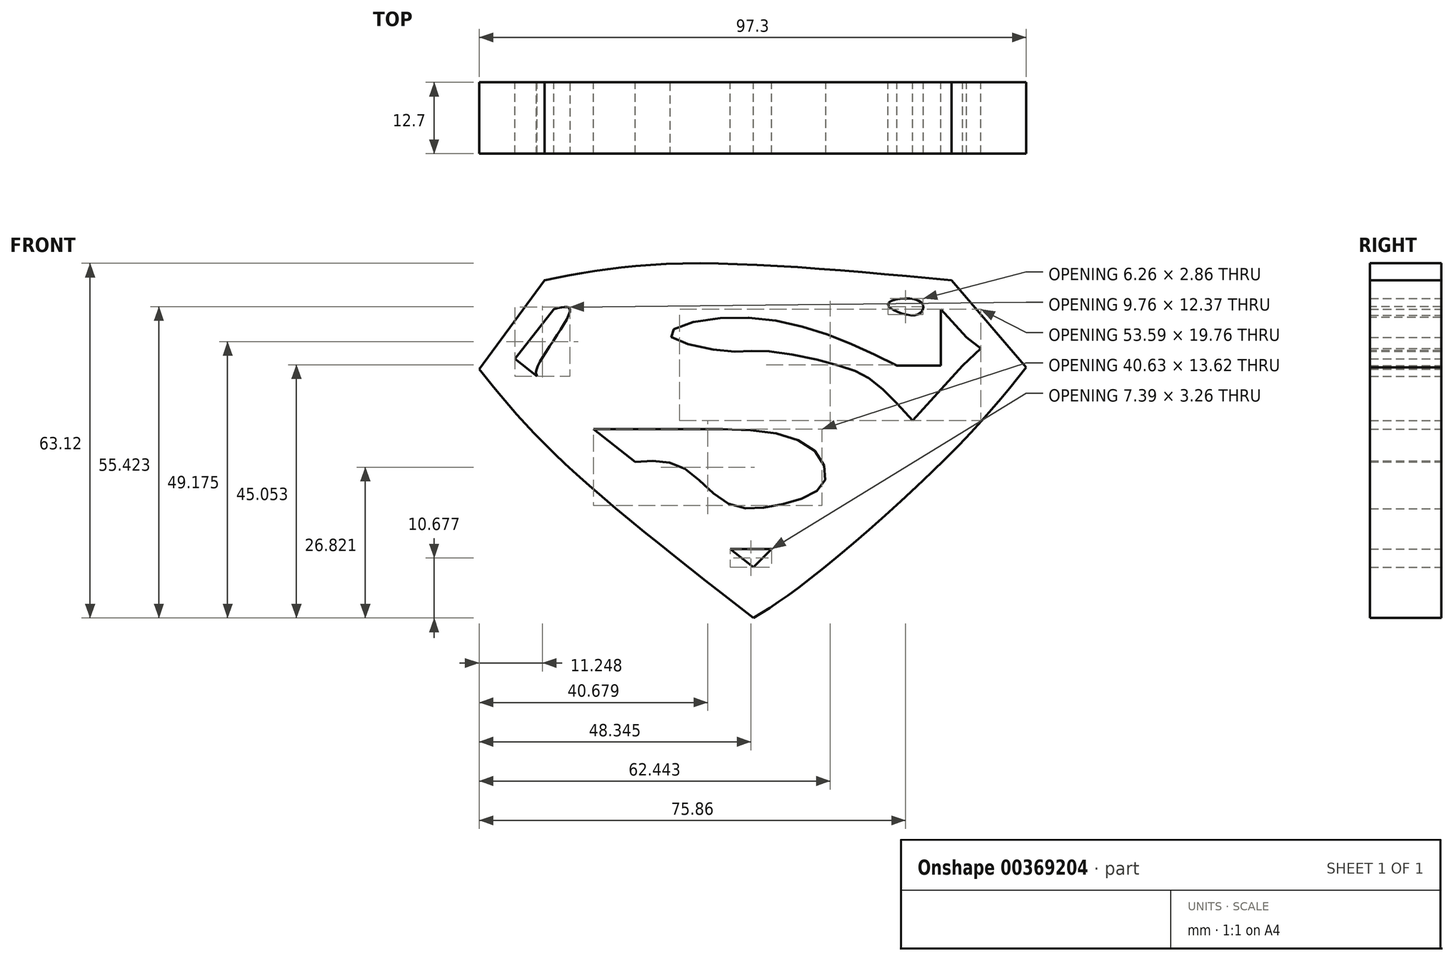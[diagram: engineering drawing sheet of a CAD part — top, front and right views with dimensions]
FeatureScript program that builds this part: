
annotation { "Feature Type Name" : "Feature", "Feature Type Description" : "" }
export const myFeature = defineFeature(function(context is Context, id is Id, definition is map)
    precondition{}
    {
        {
            var Q0;
            Q0=qCreatedBy(makeId("Front.planeOp"),FACE);
            var sketch = newSketch(context, id + "F0", { "sketchPlane" : qUnion([Q0])});
            skLineSegment(sketch, "E0", {"start": v(35.24, 21.5) * mm, "end": v(48.5, 5.98) * mm});
            skLineSegment(sketch, "E1", {"start": v(-48.81, 5.66) * mm, "end": v(-37.18, 21.5) * mm});
            skLineSegment(sketch, "E2", {"start": v(-21.01, -10.83) * mm, "end": v(-28.45, -5.01) * mm});
            skLineSegment(sketch, "E3", {"start": v(0, -29.58) * mm, "end": v(-8.32, -23.07) * mm});
            skLineSegment(sketch, "E4", {"start": v(-8.32, -23.07) * mm, "end": v(-4.16, -26.32) * mm});
            skLineSegment(sketch, "E5", {"start": v(-4.16, -26.32) * mm, "end": v(3.23, -26.32) * mm});
            skLineSegment(sketch, "E6", {"start": v(3.23, -26.32) * mm, "end": v(0, -29.58) * mm});
            skLineSegment(sketch, "E7", {"start": v(-38.47, 4.36) * mm, "end": v(-42.44, 7.47) * mm});
            skLineSegment(sketch, "E8", {"start": v(-42.44, 7.47) * mm, "end": v(-35.53, 16.3) * mm});
            skLineSegment(sketch, "E9", {"start": v(33.3, 16.3) * mm, "end": v(33.3, 6.3) * mm});
            skLineSegment(sketch, "E10", {"start": v(25.54, 6.3) * mm, "end": v(33.3, 6.3) * mm});
            skLineSegment(sketch, "E11", {"start": v(37.18, 6.3) * mm, "end": v(28.32, -3.46) * mm});
            skLineSegment(sketch, "E12", {"start": v(33.3, 16.3) * mm, "end": v(37.9, 11.3) * mm});
            skPoint(sketch, "E12.endSnap0", {"position": v(33.3, 11.3) * mm});
            skLineSegment(sketch, "E13", {"start": v(37.9, 11.3) * mm, "end": v(40.43, 9.32) * mm});
            skLineSegment(sketch, "E14", {"start": v(40.43, 9.32) * mm, "end": v(37.18, 6.3) * mm});
            skFitSpline(sketch, "E15", {"points": [v(-28.45, -5.01) * mm, v(-8.73, -5.01) * mm, v(9.7, -7.92) * mm, v(12.6, -14.39) * mm, v(5.5, -18.27) * mm, v(-4.53, -18.27) * mm, v(-12.6, -11.8) * mm, v(-21.01, -10.83) * mm], "startDerivative": vector(100.9, 0.18) * mm, "endDerivative": vector(-71.36, -5.07) * mm});
            skFitSpline(sketch, "E16", {"points": [v(25.54, 6.3) * mm, v(11.31, 12.44) * mm, v(-6.47, 14.7) * mm, v(-14.87, 11.8) * mm, v(-5.17, 8.89) * mm, v(2.26, 8.89) * mm, v(15.2, 6.3) * mm, v(21.01, 3.72) * mm, v(28.32, -3.46) * mm], "startDerivative": vector(-91.82, 45.22) * mm, "endDerivative": vector(63.05, -68.59) * mm});
            skFitSpline(sketch, "E17", {"points": [v(-37.18, 21.5) * mm, v(-14.87, 24.4) * mm, v(35.24, 21.5) * mm], "startDerivative": vector(50, 9.68) * mm, "endDerivative": vector(92.05, -8.48) * mm});
            skFitSpline(sketch, "E18", {"points": [v(-48.81, 5.66) * mm, v(-34.91, -9.86) * mm, v(0, -38.63) * mm], "startDerivative": vector(29.49, -36.38) * mm, "endDerivative": vector(65.82, -51.25) * mm});
            skFitSpline(sketch, "E19", {"points": [v(48.5, 5.98) * mm, v(35.56, -8.9) * mm, v(9.37, -32.17) * mm, v(0, -38.63) * mm], "startDerivative": vector(-33.41, -42.04) * mm, "endDerivative": vector(-32.45, -20.32) * mm});
            skFitSpline(sketch, "E20", {"points": [v(23.92, 17.3) * mm, v(29.1, 15.35) * mm, v(29.74, 17.62) * mm, v(23.92, 17.3) * mm]});
            skFitSpline(sketch, "E21", {"points": [v(-38.47, 4.36) * mm, v(-38.47, 5.98) * mm, v(-32.65, 16.3) * mm, v(-35.53, 16.3) * mm], "startDerivative": vector(-2.78, 5.46) * mm, "endDerivative": vector(-15.72, -4.38) * mm});
            skSolve(sketch);
        }
        {
            var Q0;
            Q0 = qSketchRegion(id + "F0", true);
            extrude(context, id + "F1", {"entities" : qUnion([Q0]), "depth" : 12.7 * mm});
        }
    });
